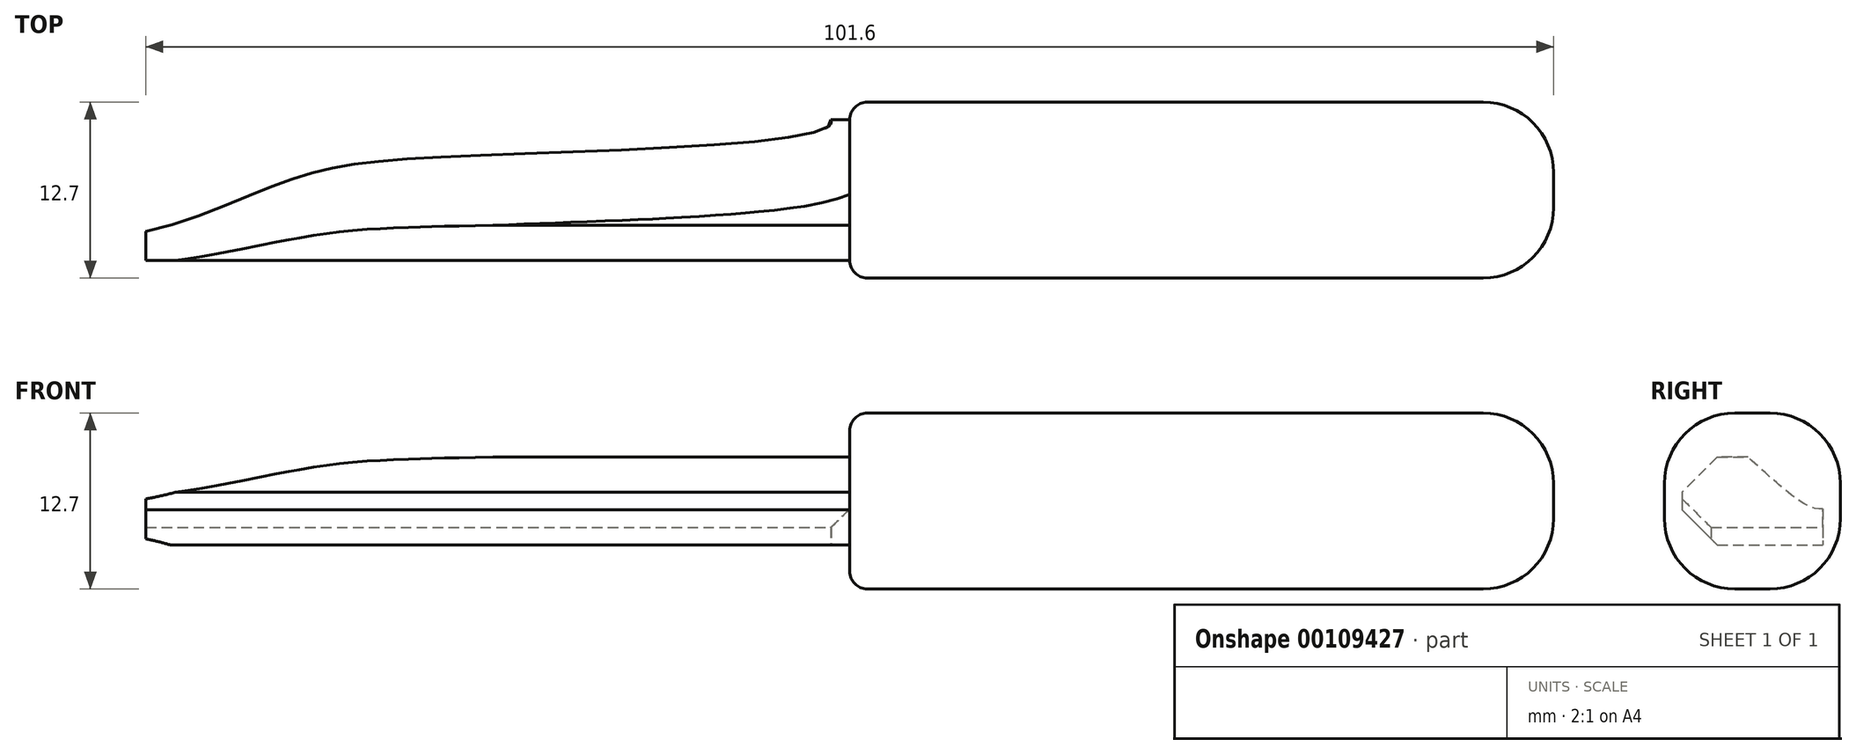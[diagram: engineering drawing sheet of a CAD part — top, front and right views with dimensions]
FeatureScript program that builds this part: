
annotation { "Feature Type Name" : "Feature", "Feature Type Description" : "" }
export const myFeature = defineFeature(function(context is Context, id is Id, definition is map)
    precondition{}
    {
        {
            var Q0;
            Q0=qCreatedBy(makeId("Front.planeOp"),FACE);
            var sketch = newSketch(context, id + "F0", { "sketchPlane" : qUnion([Q0])});
            skLineSegment(sketch, "E0.bottom", {"start": v(20.32, 6.35) * mm, "end": v(-25.4, 6.35) * mm});
            skLineSegment(sketch, "E0.top", {"start": v(20.32, -6.35) * mm, "end": v(-25.4, -6.35) * mm});
            skLineSegment(sketch, "E0.left", {"start": v(25.4, 1.27) * mm, "end": v(25.4, -1.27) * mm});
            skLineSegment(sketch, "E0.right", {"start": v(-25.4, 6.35) * mm, "end": v(-25.4, -6.35) * mm});
            skPoint(sketch, "E0.middle", {"position": v(0, 0) * mm});
            skPoint(sketch, "E1.visualSharp", {"position": v(25.4, 6.35) * mm});
            skArc(sketch, "E1.filletArc", {"start": v(25.4, 1.27) * mm, "mid": v(23.91, 4.86) * mm, "end": v(20.32, 6.35) * mm});
            skPoint(sketch, "E2.visualSharp", {"position": v(25.4, -6.35) * mm});
            skArc(sketch, "E2.filletArc", {"start": v(20.32, -6.35) * mm, "mid": v(23.91, -4.86) * mm, "end": v(25.4, -1.27) * mm});
            skSolve(sketch);
        }
        {
            var Q0;
            Q0 = qSketchRegion(id + "F0", true);
            extrude(context, id + "F1", {"entities" : qUnion([Q0]), "depth" : 6.35 * mm, "hasSecondDirection" : true, "secondDirectionOppositeDirection" : true, "secondDirectionDepth" : 6.35 * mm});
        }
        {
            var Q0;
            Q0=makeQuery(id+"F1.opExtrude","SWEPT_FACE",FACE,{"disambiguationData":[OSD([sQuery(id+"F0.wireOp",EDGE,"E0.right")])]});
            var sketch = newSketch(context, id + "F2", { "sketchPlane" : qUnion([Q0])});
            skLineSegment(sketch, "E3.bottom", {"start": v(5.08, 3.18) * mm, "end": v(-5.08, 3.18) * mm});
            skLineSegment(sketch, "E3.top", {"start": v(5.08, -3.18) * mm, "end": v(-5.08, -3.18) * mm});
            skLineSegment(sketch, "E3.left", {"start": v(5.08, 3.18) * mm, "end": v(5.08, -3.18) * mm});
            skLineSegment(sketch, "E3.right", {"start": v(-5.08, 3.18) * mm, "end": v(-5.08, -3.18) * mm});
            skPoint(sketch, "E3.middle", {"position": v(0, 0) * mm});
            skSolve(sketch);
        }
        {
            var Q0;
            Q0 = qSketchRegion(id + "F2", true);
            extrude(context, id + "F3", {"entities" : qUnion([Q0]), "depth" : 50.8 * mm});
        }
        {
            var Q0;
            Q0=makeQuery(id+"F1.opExtrude","CAP_EDGE",EDGE,{"disambiguationData":[OSD([sQuery(id+"F0.wireOp",EDGE,"E0.top")])],"isStart":false});
            var Q1;
            Q1=makeQuery(id+"F1.opExtrude","CAP_EDGE",EDGE,{"disambiguationData":[OSD([sQuery(id+"F0.wireOp",EDGE,"E0.top")])],"isStart":true});
            fillet(context, id + "F4", {"entities" : qUnion([Q0, Q1]), "radius" : 5.08 * mm, "tangentPropagation" : true, "allowEdgeOverflow" : false});
        }
        {
            var Q0;
            Q0=makeQuery(id+"F3.opExtrude","SWEPT_EDGE",EDGE,{"disambiguationData":[OSD([sQuery(id+"F2.wireOp",EDGE,"E3.top"),sQuery(id+"F2.wireOp",EDGE,"E3.left")])]});
            var Q1;
            Q1=makeQuery(id+"F3.opExtrude","SWEPT_EDGE",EDGE,{"disambiguationData":[OSD([sQuery(id+"F2.wireOp",EDGE,"E3.bottom"),sQuery(id+"F2.wireOp",EDGE,"E3.left")])]});
            chamfer(context, id + "F5", {"entities" : qUnion([Q0, Q1]), "width" : 2.54 * mm, "tangentPropagation" : true});
        }
        {
            var Q0;
            Q0=makeQuery(id+"F3.opExtrude","SWEPT_FACE",FACE,{"disambiguationData":[OSD([sQuery(id+"F2.wireOp",EDGE,"E3.top")])]});
            var sketch = newSketch(context, id + "F6", { "sketchPlane" : qUnion([Q0])});
            skFitSpline(sketch, "E4", {"points": [v(-80.77, 2.54) * mm, v(-67.78, 0) * mm, v(-54.59, -2.4) * mm, v(-26.78, -5.08) * mm, v(-79.25, -7.18) * mm, v(-80.77, 2.54) * mm]});
            skSolve(sketch);
        }
        {
            var Q0;
            Q0 = qSketchRegion(id + "F6", true);
            extrude(context, id + "F7", {"entities" : qUnion([Q0]), "operationType" : NewBodyOperationType.REMOVE, "oppositeDirection" : true, "depth" : 25.4 * mm});
        }
        {
            var Q0;
            Q0=makeQuery(id+"F7.boolean.opBoolean","COPY",EDGE,{"derivedFrom":makeQuery(id+"F7.opExtrude","CAP_EDGE",EDGE,{"disambiguationData":[OSD([sQuery(id+"F6.wireOp",EDGE,"E4")])],"isStart":true})});
            var Q1;
            Q1=makeQuery(id+"F7.boolean.opBoolean","INTERSECT",EDGE,{"derivedFrom":[makeQuery(id+"F3.opExtrude","SWEPT_FACE",FACE,{"disambiguationData":[OSD([sQuery(id+"F2.wireOp",EDGE,"E3.bottom")])]}),makeQuery(id+"F7.opExtrude","SWEPT_FACE",FACE,{"disambiguationData":[OSD([sQuery(id+"F6.wireOp",EDGE,"E4")])]})]});
            chamfer(context, id + "F8", {"entities" : qUnion([Q0, Q1]), "width" : 5.08 * mm, "tangentPropagation" : true});
        }
        {
            var Q0;
            Q0=makeQuery(id+"F4.opFillet","BLEND_EDGE",EDGE,{"blendedFrom":[makeQuery(id+"F1.opExtrude","CAP_EDGE",EDGE,{"disambiguationData":[OSD([sQuery(id+"F0.wireOp",EDGE,"E0.top")])],"isStart":false}),makeQuery(id+"F1.opExtrude","SWEPT_FACE",FACE,{"disambiguationData":[OSD([sQuery(id+"F0.wireOp",EDGE,"E0.right")])]})],"blendedInto":[makeQuery(id+"F1.opExtrude","SWEPT_FACE",FACE,{"disambiguationData":[OSD([sQuery(id+"F0.wireOp",EDGE,"E0.right")])]})]});
            fillet(context, id + "F9", {"entities" : qUnion([Q0]), "radius" : 1.27 * mm, "tangentPropagation" : true, "allowEdgeOverflow" : false});
        }
    });
